# Revit family: Sanitary_Accessories_Sanindusa_New-WC-Care-Pneumatic-Fixation-For-65-Washbasin
name_source: partatom
category: Plumbing Fixtures
revit_build: Autodesk Revit 2018 (Build: 20170223_1515(x64)
units: mm (PartAtom-declared; Revit-internal decimal feet)

## family parameters
Always vertical = Yes
Cut with Voids When Loaded = No
Host = Wall
OmniClass Number = 23.45.00.00
OmniClass Title = Sanitary, Laundry, and Cleaning Equipment
Part Type = Normal
Room Calculation Point = No
Round Connector Dimension = Use Diameter
Shared = No

## types (1)
- Sanindusa
    AssetType = Fixed
    BarCode = 5604815899597
    Color = white
    Constituents = Includes fixing kit for brick walls and for fixing the washbasin
the structure.
Supporting frame for mounting; Height adjustable galvanized support legs; Depth adjustable galvanised brackets for pre-wall installation; Two threaded rods with M10 nuts for attaching bidet; Height adjustable PE drain elbow ø 50 mm; Rubber sink trap seal, ø 32 mm; Other parts necessary to fix and connect the product.
Supporting frame for mounting; Height adjustable galvanized support legs; Depth adjustable galvanised brackets for pre-wall installation; Two threaded rods with M10 nuts for attaching bidet; Height adjustable PE drain elbow ø 50 mm; Rubber sink trap seal, ø 32 mm; Other parts necessary to fix and connect the product.
    Cost = 0 $
    D = 800 mm  [stored 2.62467 ft]
    Description = Pneumatic fixation for washbasin
    Edition number = 1
    Features = Smooth and silent movement.
Two-way tilt locking system.
Pneumatic cylinder activated by lever.
    Finish = white powder coating
    Installation Instructions = https://www.tec.sanindusa.pt
    Manufacturer = www.sanindusa.pt
    ManufacturerName = Sanindusa
    ManufacturerURL = www.tec.sanindusa.pt
    Material = Carbon steel
    ModelNumber = 4290200
    ModelReference = New Wccare
    Name = Pneumatic fixation for washbasin new wccare 65
    NominalHeight = 345 mm  [stored 1.13189 ft]
    NominalLength = 651 mm  [stored 2.13583 ft]
    NominalWidth = 350 mm  [stored 1.14829 ft]
    Product Guid = 5b42c11c-954c-4be1-9a2e-2b2f414ab29f
    Product data url = https://bimobject.com
    ProductInformation = https://www.tec.sanindusa.pt
    Size = 65x35
    URL = www.tec.sanindusa.pt
    Uniclass2015Code = Pr_40_20_76_84
    Uniclass2015Title = Support rails
    Uniclass2015Version = Products v1.6
    Version = 2
    WarrantyDescription = https://www.tec.sanindusa.pt
The warranty will come into force from the moment the warranty detachable bulletin that accompanies the product is received at Sanindusa or from the moment the product is sold to the distributer
Only if the customer issues a writen and justified (Country laws, state laws, commercial strategy) request to Sanindusa, may the above mentioned warranties be the object of a possible change.
The warranty will come into force from the moment the warranty detachable bulletin that accompanies the product is received at Sanindusa or from the moment the product is sold to the distributer
Only if the customer issues a writen and justified (Country laws, state laws, commercial strategy) request to Sanindusa, may the above mentioned warranties be the object of a possible change.
    WarrantyDurationParts = 5
    WarrantyDurationUnit = year
    WarrantyStartDate = 1900-12-31T23:59:59
    Weight = 7.70 kg

note: [stored X ft] marks values corroborated as IEEE doubles in the binary element streams (Revit-internal decimal feet)

## geometry (parser evidence)
native form markers: Sweep x7
no freeform markers — native parametric forms only
